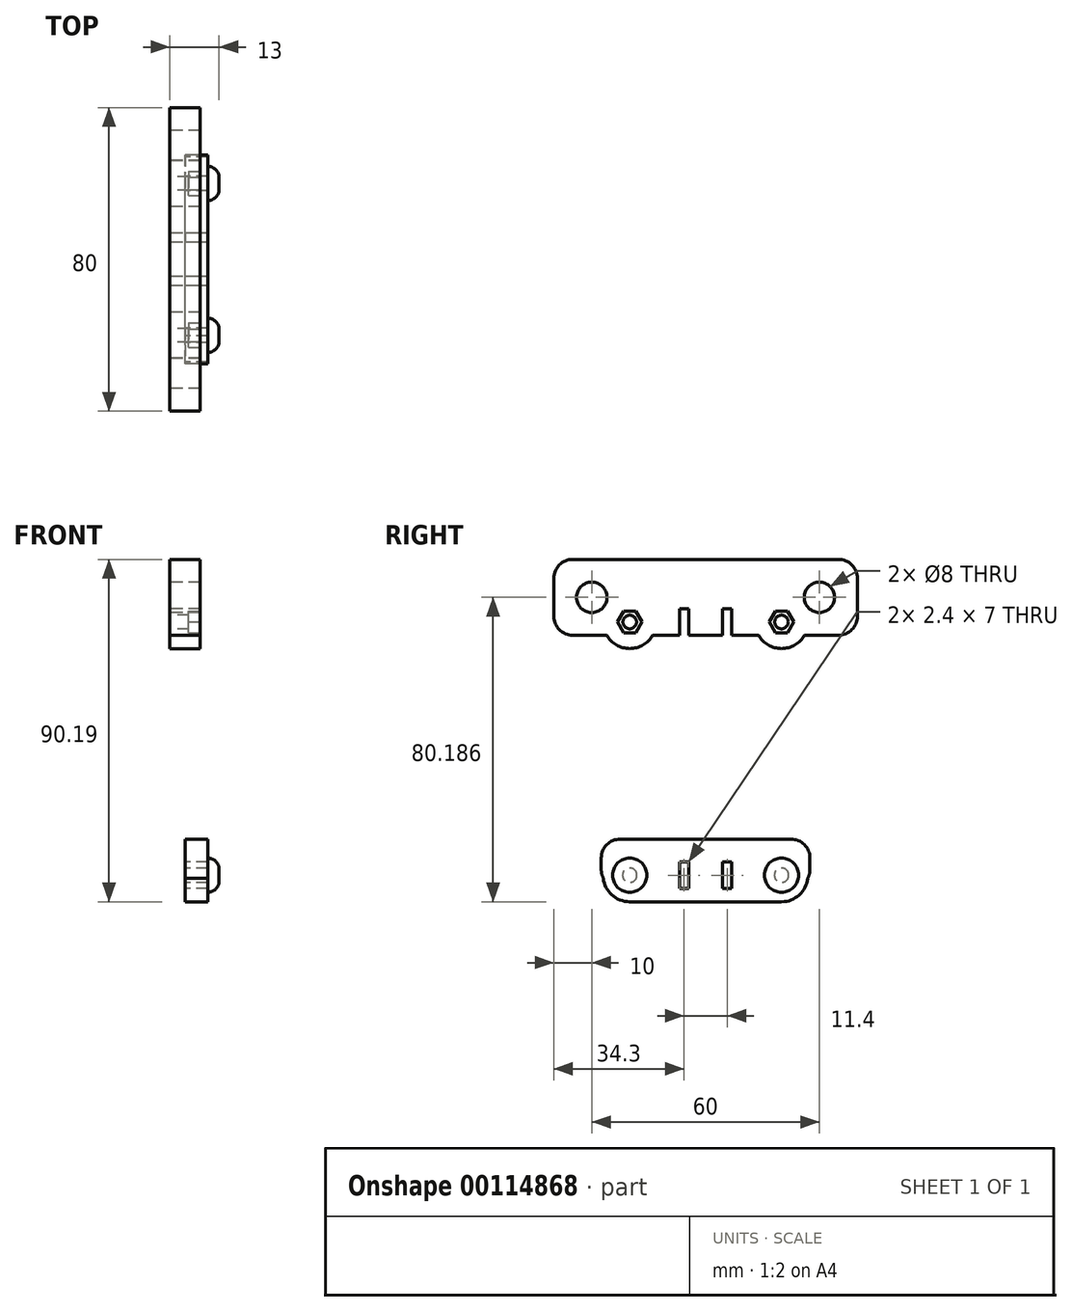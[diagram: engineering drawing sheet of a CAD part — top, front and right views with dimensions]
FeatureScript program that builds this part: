
annotation { "Feature Type Name" : "Feature", "Feature Type Description" : "" }
export const myFeature = defineFeature(function(context is Context, id is Id, definition is map)
    precondition{}
    {
        {
            var Q0;
            Q0=qCreatedBy(makeId("Right.planeOp"),FACE);
            var sketch = newSketch(context, id + "F0", { "sketchPlane" : qUnion([Q0])});
            skLineSegment(sketch, "E0", {"start": v(0, 142.5) * mm, "end": v(0, -139.74) * mm, "construction": true});
            skLineSegment(sketch, "E1.bottom", {"start": v(-35, 25) * mm, "end": v(35, 25) * mm});
            skLineSegment(sketch, "E1.top", {"start": v(-40, -25) * mm, "end": v(40, -25) * mm});
            skLineSegment(sketch, "E1.left", {"start": v(-40, 20) * mm, "end": v(-40, -25) * mm});
            skLineSegment(sketch, "E1.right", {"start": v(40, 20) * mm, "end": v(40, -25) * mm});
            skPoint(sketch, "E1.middle", {"position": v(0, 0) * mm});
            skCircle(sketch, "E2", {"center": v(-30, 13) * mm, "radius": 4 * mm});
            skCircle(sketch, "E3", {"center": v(30, 13) * mm, "radius": 4 * mm});
            skCircle(sketch, "E4", {"center": v(-30, -13) * mm, "radius": 5 * mm});
            skCircle(sketch, "E5", {"center": v(30, -13) * mm, "radius": 5 * mm});
            skPoint(sketch, "E6.visualSharp", {"position": v(-40, 25) * mm});
            skArc(sketch, "E6.filletArc", {"start": v(-35, 25) * mm, "mid": v(-38.54, 23.54) * mm, "end": v(-40, 20) * mm});
            skPoint(sketch, "E7.visualSharp", {"position": v(40, 25) * mm});
            skArc(sketch, "E7.filletArc", {"start": v(40, 20) * mm, "mid": v(38.54, 23.54) * mm, "end": v(35, 25) * mm});
            skLineSegment(sketch, "E8.bottom", {"start": v(-11, 25) * mm, "end": v(11, 25) * mm});
            skLineSegment(sketch, "E8.top", {"start": v(-9, 8) * mm, "end": v(9, 8) * mm});
            skLineSegment(sketch, "E8.left", {"start": v(-11, 25) * mm, "end": v(-11, 10) * mm});
            skLineSegment(sketch, "E8.right", {"start": v(11, 25) * mm, "end": v(11, 10) * mm});
            skPoint(sketch, "E8.middle", {"position": v(0, 16.5) * mm});
            skPoint(sketch, "E9.visualSharp", {"position": v(11, 8) * mm});
            skArc(sketch, "E9.filletArc", {"start": v(9, 8) * mm, "mid": v(10.41, 8.59) * mm, "end": v(11, 10) * mm});
            skPoint(sketch, "E10.visualSharp", {"position": v(-11, 8) * mm});
            skArc(sketch, "E10.filletArc", {"start": v(-11, 10) * mm, "mid": v(-10.41, 8.59) * mm, "end": v(-9, 8) * mm});
            skSolve(sketch);
        }
        {
            var Q0;
            Q0=makeQuery(id+"F0.imprint","IMPRINT",FACE,{"disambiguationData":[TD([[makeQuery(id+"F0.imprint","IMPRINT",EDGE,{"derivedFrom":sQuery(id+"F0.wireOp",EDGE,"E1.bottom")}),-1.0]])]});
            extrude(context, id + "F1", {"entities" : qUnion([Q0]), "endBound" : BoundingType.SYMMETRIC, "depth" : 8 * mm});
        }
        {
            var Q0;
            {var subQ0=sQuery(id+"F0.wireOp",EDGE,"E1.bottom");Q0=makeQuery(id+"F1.opExtrude","SWEPT_FACE",FACE,{"disambiguationData":[OSD([subQ0]),TDD([makeQuery(id+"F0.imprint","IMPRINT",EDGE,{"disambiguationData":[TD([[makeQuery(id+"F0.imprint","INTERSECT",VERTEX,{"derivedFrom":[subQ0,sQuery(id+"F0.wireOp",EDGE,"E7.filletArc")]}),1.0]])],"derivedFrom":subQ0})])]});}
            var sketch = newSketch(context, id + "F2", { "sketchPlane" : qUnion([Q0])});
            skCircle(sketch, "E11", {"center": v(0, 30) * mm, "radius": 1.4 * mm});
            skCircle(sketch, "E12", {"center": v(0, 24) * mm, "radius": 1.4 * mm});
            skCircle(sketch, "E13", {"center": v(0, -24) * mm, "radius": 1.4 * mm});
            skCircle(sketch, "E14", {"center": v(0, -30) * mm, "radius": 1.4 * mm});
            skLineSegment(sketch, "E15", {"start": v(-76.86, 0) * mm, "end": v(82.98, 0) * mm, "construction": true});
            skSolve(sketch);
        }
        {
            var Q0;
            Q0=qSketchRegion(id+"F2",true);
            extrude(context, id + "F3", {"entities" : qUnion([Q0]), "operationType" : NewBodyOperationType.REMOVE, "oppositeDirection" : true, "depth" : 13 * mm});
        }
        {
            var Q0;
            Q0=qCreatedBy(makeId("Right.planeOp"),FACE);
            var sketch = newSketch(context, id + "F4", { "sketchPlane" : qUnion([Q0])});
            skLineSegment(sketch, "E16", {"start": v(0, 90) * mm, "end": v(0, 27.03) * mm, "construction": true});
            skCircle(sketch, "E17", {"center": v(-30, 70.19) * mm, "radius": 4 * mm});
            skCircle(sketch, "E18", {"center": v(30, 70.19) * mm, "radius": 4 * mm});
            skLineSegment(sketch, "E19.bottom", {"start": v(-35, 80.19) * mm, "end": v(35, 80.19) * mm});
            skLineSegment(sketch, "E19.top", {"start": v(-35, 60.19) * mm, "end": v(-26.06, 60.19) * mm});
            skLineSegment(sketch, "E19.left", {"start": v(-40, 75.19) * mm, "end": v(-40, 65.19) * mm});
            skLineSegment(sketch, "E19.right", {"start": v(40, 75.19) * mm, "end": v(40, 65.19) * mm});
            skPoint(sketch, "E19.middle", {"position": v(0, 70.19) * mm});
            skPoint(sketch, "E20.visualSharp", {"position": v(-40, 80.19) * mm});
            skArc(sketch, "E20.filletArc", {"start": v(-35, 80.19) * mm, "mid": v(-38.54, 78.72) * mm, "end": v(-40, 75.19) * mm});
            skPoint(sketch, "E21.visualSharp", {"position": v(-40, 60.19) * mm});
            skArc(sketch, "E21.filletArc", {"start": v(-40, 65.19) * mm, "mid": v(-38.54, 61.65) * mm, "end": v(-35, 60.19) * mm});
            skPoint(sketch, "E22.visualSharp", {"position": v(40, 80.19) * mm});
            skArc(sketch, "E22.filletArc", {"start": v(40, 75.19) * mm, "mid": v(38.54, 78.72) * mm, "end": v(35, 80.19) * mm});
            skPoint(sketch, "E23.visualSharp", {"position": v(40, 60.19) * mm});
            skArc(sketch, "E23.filletArc", {"start": v(35, 60.19) * mm, "mid": v(38.54, 61.65) * mm, "end": v(40, 65.19) * mm});
            skLineSegment(sketch, "E24.bottom", {"start": v(-11, 80.19) * mm, "end": v(11, 80.19) * mm});
            skPoint(sketch, "E24.middle", {"position": v(0, 76.69) * mm});
            skLineSegment(sketch, "E25", {"start": v(-87.97, 70.19) * mm, "end": v(-87.97, 70.19) * mm});
            skPoint(sketch, "E25.endSnap0", {"position": v(40, 70.19) * mm});
            skLineSegment(sketch, "E26.bottom", {"start": v(-6.9, 67.19) * mm, "end": v(-4.5, 67.19) * mm});
            skLineSegment(sketch, "E26.top", {"start": v(-6.9, 60.19) * mm, "end": v(-4.5, 60.19) * mm});
            skLineSegment(sketch, "E26.left", {"start": v(-6.9, 67.19) * mm, "end": v(-6.9, 60.19) * mm});
            skLineSegment(sketch, "E26.right", {"start": v(-4.5, 67.19) * mm, "end": v(-4.5, 60.19) * mm});
            skLineSegment(sketch, "E27.bottom", {"start": v(4.5, 67.19) * mm, "end": v(6.9, 67.19) * mm});
            skLineSegment(sketch, "E27.top", {"start": v(4.5, 60.19) * mm, "end": v(6.9, 60.19) * mm});
            skLineSegment(sketch, "E27.left", {"start": v(4.5, 67.19) * mm, "end": v(4.5, 60.19) * mm});
            skLineSegment(sketch, "E27.right", {"start": v(6.9, 67.19) * mm, "end": v(6.9, 60.19) * mm});
            skCircle(sketch, "E28", {"center": v(-20, 63.69) * mm, "radius": 1.8 * mm});
            skCircle(sketch, "E29", {"center": v(20, 63.69) * mm, "radius": 1.8 * mm});
            skArc(sketch, "E30", {"start": v(-26.06, 60.19) * mm, "mid": v(-20, 56.69) * mm, "end": v(-13.94, 60.19) * mm});
            skArc(sketch, "E31.MirrorC", {"start": v(26.06, 60.19) * mm, "mid": v(20, 56.69) * mm, "end": v(13.94, 60.19) * mm});
            skLineSegment(sketch, "E32.trimOffspring", {"start": v(-13.94, 60.19) * mm, "end": v(13.94, 60.19) * mm});
            skLineSegment(sketch, "E33.trimOffspring", {"start": v(26.06, 60.19) * mm, "end": v(35, 60.19) * mm});
            skSolve(sketch);
        }
        {
            var Q0;
            Q0=makeQuery(id+"F4.imprint","IMPRINT",FACE,{"disambiguationData":[TD([[makeQuery(id+"F4.imprint","IMPRINT",EDGE,{"derivedFrom":sQuery(id+"F4.wireOp",EDGE,"E17")}),-1.0]])]});
            extrude(context, id + "F5", {"entities" : qUnion([Q0]), "endBound" : BoundingType.SYMMETRIC, "depth" : 8 * mm});
        }
        {
            var Q0;
            Q0=makeQuery(id+"F5.opExtrude","CAP_FACE",FACE,{"disambiguationData":[OSD([sQuery(id+"F4.wireOp",EDGE,"E17"),sQuery(id+"F4.wireOp",EDGE,"E18"),sQuery(id+"F4.wireOp",EDGE,"E19.bottom"),sQuery(id+"F4.wireOp",EDGE,"E19.top"),sQuery(id+"F4.wireOp",EDGE,"E19.left"),sQuery(id+"F4.wireOp",EDGE,"E19.right"),sQuery(id+"F4.wireOp",EDGE,"E20.filletArc"),sQuery(id+"F4.wireOp",EDGE,"E21.filletArc"),sQuery(id+"F4.wireOp",EDGE,"E22.filletArc"),sQuery(id+"F4.wireOp",EDGE,"E23.filletArc"),sQuery(id+"F4.wireOp",EDGE,"E24.bottom"),sQuery(id+"F4.wireOp",EDGE,"E26.bottom"),sQuery(id+"F4.wireOp",EDGE,"E26.left"),sQuery(id+"F4.wireOp",EDGE,"E26.right"),sQuery(id+"F4.wireOp",EDGE,"E27.bottom"),sQuery(id+"F4.wireOp",EDGE,"E27.left"),sQuery(id+"F4.wireOp",EDGE,"E27.right"),sQuery(id+"F4.wireOp",EDGE,"E28"),sQuery(id+"F4.wireOp",EDGE,"E29")])],"isStart":false});
            var sketch = newSketch(context, id + "F6", { "sketchPlane" : qUnion([Q0])});
            skCircle(sketch, "E34.cCircle", {"center": v(20, 63.69) * mm, "radius": 2.8 * mm, "construction": true});
            skLineSegment(sketch, "E34.0", {"start": v(18.38, 66.49) * mm, "end": v(21.62, 66.49) * mm});
            skLineSegment(sketch, "E34.1", {"start": v(21.62, 66.49) * mm, "end": v(23.23, 63.69) * mm});
            skLineSegment(sketch, "E34.2", {"start": v(23.23, 63.69) * mm, "end": v(21.62, 60.89) * mm});
            skLineSegment(sketch, "E34.3", {"start": v(21.62, 60.89) * mm, "end": v(18.38, 60.89) * mm});
            skLineSegment(sketch, "E34.4", {"start": v(18.38, 60.89) * mm, "end": v(16.77, 63.69) * mm});
            skLineSegment(sketch, "E34.5", {"start": v(16.77, 63.69) * mm, "end": v(18.38, 66.49) * mm});
            skPoint(sketch, "E34.0.midPoint", {"position": v(20, 66.49) * mm});
            skCircle(sketch, "E35.cCircle", {"center": v(-20, 63.69) * mm, "radius": 2.8 * mm, "construction": true});
            skLineSegment(sketch, "E35.0", {"start": v(-21.62, 66.49) * mm, "end": v(-18.38, 66.49) * mm});
            skLineSegment(sketch, "E35.1", {"start": v(-18.38, 66.49) * mm, "end": v(-16.77, 63.69) * mm});
            skLineSegment(sketch, "E35.2", {"start": v(-16.77, 63.69) * mm, "end": v(-18.38, 60.89) * mm});
            skLineSegment(sketch, "E35.3", {"start": v(-18.38, 60.89) * mm, "end": v(-21.62, 60.89) * mm});
            skLineSegment(sketch, "E35.4", {"start": v(-21.62, 60.89) * mm, "end": v(-23.23, 63.69) * mm});
            skLineSegment(sketch, "E35.5", {"start": v(-23.23, 63.69) * mm, "end": v(-21.62, 66.49) * mm});
            skPoint(sketch, "E35.0.midPoint", {"position": v(-20, 66.49) * mm});
            skSolve(sketch);
        }
        {
            var Q0;
            Q0 = qSketchRegion(id + "F6", true);
            extrude(context, id + "F7", {"entities" : qUnion([Q0]), "operationType" : NewBodyOperationType.REMOVE, "oppositeDirection" : true, "depth" : 3 * mm});
        }
        {
            var Q0;
            Q0=qCreatedBy(makeId("Right.planeOp"),FACE);
            var sketch = newSketch(context, id + "F8", { "sketchPlane" : qUnion([Q0])});
            skLineSegment(sketch, "E36.bottom", {"start": v(-22.5, 6.5) * mm, "end": v(22.5, 6.5) * mm});
            skLineSegment(sketch, "E36.top", {"start": v(-6.9, -6.5) * mm, "end": v(-4.5, -6.5) * mm});
            skLineSegment(sketch, "E36.left", {"start": v(-27.5, 1.5) * mm, "end": v(-27.5, -1.5) * mm});
            skLineSegment(sketch, "E36.right", {"start": v(27.5, 1.5) * mm, "end": v(27.5, -1.5) * mm});
            skPoint(sketch, "E36.middle", {"position": v(0, 0) * mm});
            skPoint(sketch, "E37.visualSharp", {"position": v(-27.5, 6.5) * mm});
            skArc(sketch, "E37.filletArc", {"start": v(-22.5, 6.5) * mm, "mid": v(-26.04, 5.04) * mm, "end": v(-27.5, 1.5) * mm});
            skPoint(sketch, "E38.visualSharp", {"position": v(-27.5, -6.5) * mm});
            skArc(sketch, "E38.filletArc", {"start": v(-27.5, -1.5) * mm, "mid": v(-27.36, -2.66) * mm, "end": v(-26.96, -3.76) * mm});
            skPoint(sketch, "E39.visualSharp", {"position": v(27.5, 6.5) * mm});
            skArc(sketch, "E39.filletArc", {"start": v(27.5, 1.5) * mm, "mid": v(26.04, 5.04) * mm, "end": v(22.5, 6.5) * mm});
            skPoint(sketch, "E40.visualSharp", {"position": v(27.5, -6.5) * mm});
            skArc(sketch, "E40.filletArc", {"start": v(26.96, -3.76) * mm, "mid": v(27.36, -2.66) * mm, "end": v(27.5, -1.5) * mm});
            skLineSegment(sketch, "E41.bottom", {"start": v(-6.9, 0.5) * mm, "end": v(-4.5, 0.5) * mm});
            skLineSegment(sketch, "E41.left", {"start": v(-6.9, 0.5) * mm, "end": v(-6.9, -6.5) * mm});
            skLineSegment(sketch, "E41.right", {"start": v(-4.5, 0.5) * mm, "end": v(-4.5, -6.5) * mm});
            skLineSegment(sketch, "E42.MirrorCS", {"start": v(6.9, 0.5) * mm, "end": v(4.5, 0.5) * mm});
            skLineSegment(sketch, "E43.MirrorCS", {"start": v(6.9, -6.5) * mm, "end": v(4.5, -6.5) * mm});
            skLineSegment(sketch, "E44.MirrorCS", {"start": v(4.5, 0.5) * mm, "end": v(4.5, -6.5) * mm});
            skLineSegment(sketch, "E45.MirrorCS", {"start": v(6.9, 0.5) * mm, "end": v(6.9, -6.5) * mm});
            skCircle(sketch, "E46", {"center": v(20, -3) * mm, "radius": 1.9 * mm});
            skCircle(sketch, "E47.MirrorC", {"center": v(-20, -3) * mm, "radius": 1.9 * mm});
            skArc(sketch, "E48", {"start": v(-26.96, -3.76) * mm, "mid": v(-24.64, -8.24) * mm, "end": v(-19.91, -10) * mm});
            skArc(sketch, "E49.MirrorC", {"start": v(26.96, -3.76) * mm, "mid": v(24.67, -8.21) * mm, "end": v(20, -10) * mm});
            skPoint(sketch, "E50.orphan", {"position": v(22.5, -6.5) * mm});
            skLineSegment(sketch, "E51", {"start": v(-20.09, -10) * mm, "end": v(20, -10) * mm});
            skLineSegment(sketch, "E52.trimOffspring", {"start": v(4.5, -6.5) * mm, "end": v(6.9, -6.5) * mm});
            skSolve(sketch);
        }
        {
            var Q0;
            Q0=makeQuery(id+"F8.imprint","IMPRINT",FACE,{"disambiguationData":[TD([[makeQuery(id+"F8.imprint","IMPRINT",EDGE,{"derivedFrom":sQuery(id+"F8.wireOp",EDGE,"E36.bottom")}),-1.0]])]});
            extrude(context, id + "F9", {"entities" : qUnion([Q0]), "depth" : 6 * mm});
        }
        {
            var Q0;
            Q0=makeQuery(id+"F1.opExtrude","SWEPT_BODY",BODY,{"disambiguationData":[OSD([sQuery(id+"F0.wireOp",EDGE,"E1.bottom"),sQuery(id+"F0.wireOp",EDGE,"E1.top"),sQuery(id+"F0.wireOp",EDGE,"E1.left"),sQuery(id+"F0.wireOp",EDGE,"E1.right"),sQuery(id+"F0.wireOp",EDGE,"E2"),sQuery(id+"F0.wireOp",EDGE,"E3"),sQuery(id+"F0.wireOp",EDGE,"E4"),sQuery(id+"F0.wireOp",EDGE,"E5"),sQuery(id+"F0.wireOp",EDGE,"E6.filletArc"),sQuery(id+"F0.wireOp",EDGE,"E7.filletArc"),sQuery(id+"F0.wireOp",EDGE,"E8.top"),sQuery(id+"F0.wireOp",EDGE,"E8.left"),sQuery(id+"F0.wireOp",EDGE,"E8.right"),sQuery(id+"F0.wireOp",EDGE,"E9.filletArc"),sQuery(id+"F0.wireOp",EDGE,"E10.filletArc")])]});
            deleteBodies(context, id + "F10", {"entities" : qUnion([Q0])});
        }
        {
            var Q0;
            Q0=makeQuery(id+"F9.opExtrude","CAP_FACE",FACE,{"disambiguationData":[OSD([sQuery(id+"F8.wireOp",EDGE,"E36.bottom"),sQuery(id+"F8.wireOp",EDGE,"E36.top"),sQuery(id+"F8.wireOp",EDGE,"E36.left"),sQuery(id+"F8.wireOp",EDGE,"E36.right"),sQuery(id+"F8.wireOp",EDGE,"E37.filletArc"),sQuery(id+"F8.wireOp",EDGE,"E38.filletArc"),sQuery(id+"F8.wireOp",EDGE,"E39.filletArc"),sQuery(id+"F8.wireOp",EDGE,"E40.filletArc"),sQuery(id+"F8.wireOp",EDGE,"E41.bottom"),sQuery(id+"F8.wireOp",EDGE,"E41.left"),sQuery(id+"F8.wireOp",EDGE,"E41.right"),sQuery(id+"F8.wireOp",EDGE,"E42.MirrorCS"),sQuery(id+"F8.wireOp",EDGE,"E44.MirrorCS"),sQuery(id+"F8.wireOp",EDGE,"E45.MirrorCS"),sQuery(id+"F8.wireOp",EDGE,"E46"),sQuery(id+"F8.wireOp",EDGE,"E47.MirrorC")])],"isStart":false});
            var sketch = newSketch(context, id + "F11", { "sketchPlane" : qUnion([Q0])});
            skCircle(sketch, "E53", {"center": v(-20, -3) * mm, "radius": 4.5 * mm});
            skCircle(sketch, "E54.MirrorC", {"center": v(20, -3) * mm, "radius": 4.5 * mm});
            skSolve(sketch);
        }
        {
            var Q0;
            Q0 = qSketchRegion(id + "F11", true);
            extrude(context, id + "F12", {"entities" : qUnion([Q0]), "operationType" : NewBodyOperationType.ADD, "depth" : 3 * mm});
        }
        {
            var Q0;
            Q0=makeQuery(id+"F12.opExtrude","CAP_EDGE",EDGE,{"disambiguationData":[OSD([sQuery(id+"F11.wireOp",EDGE,"E53")])],"isStart":false});
            var Q1;
            Q1=makeQuery(id+"F12.opExtrude","CAP_EDGE",EDGE,{"disambiguationData":[OSD([sQuery(id+"F11.wireOp",EDGE,"E54.MirrorC")])],"isStart":false});
            fillet(context, id + "F13", {"entities" : qUnion([Q0, Q1]), "radius" : 3 * mm, "tangentPropagation" : true, "allowEdgeOverflow" : false});
        }
    });
